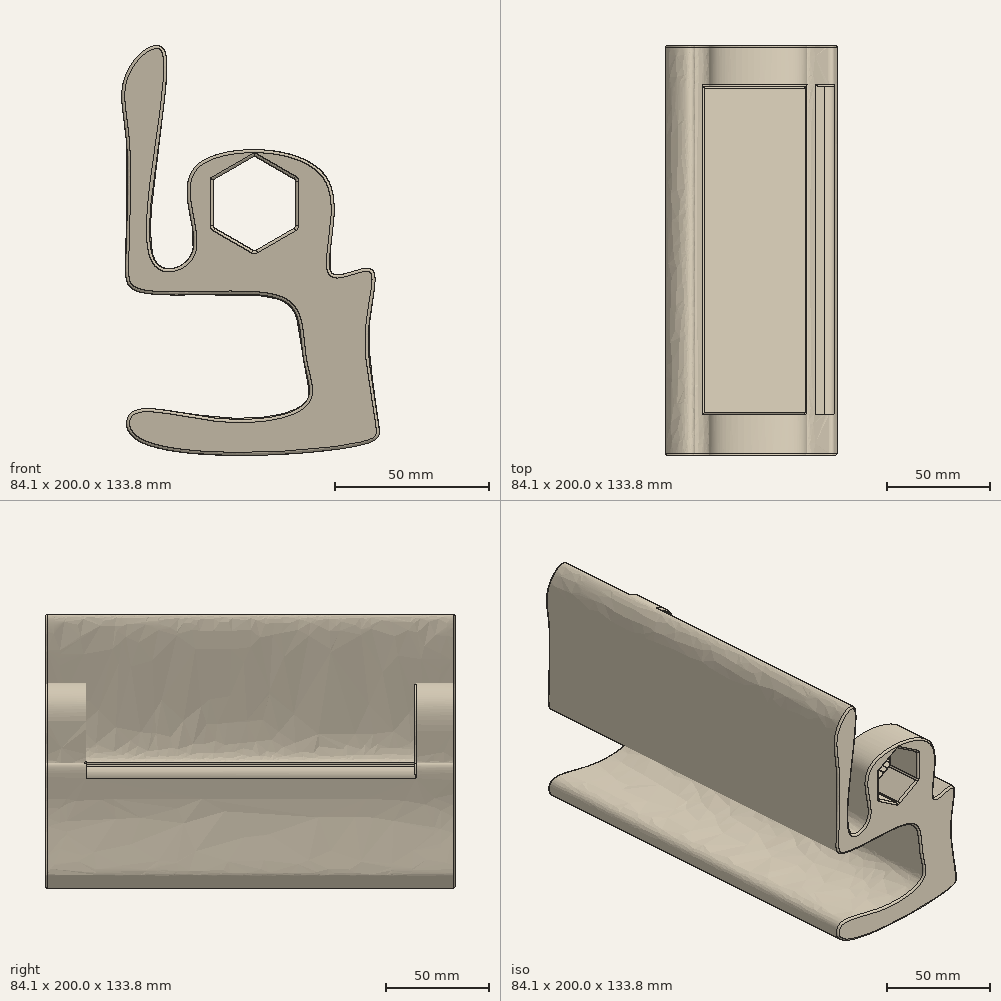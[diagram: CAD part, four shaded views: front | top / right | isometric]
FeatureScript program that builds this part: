
annotation { "Feature Type Name" : "Feature", "Feature Type Description" : "" }
export const myFeature = defineFeature(function(context is Context, id is Id, definition is map)
    precondition{}
    {
        {
            var Q0;
            Q0=qCreatedBy(makeId("Front.planeOp"),FACE);
            var sketch = newSketch(context, id + "F0", { "sketchPlane" : qUnion([Q0])});
            skFitSpline(sketch, "E0", {"points": [v(-28.85, 42.52) * mm, v(-29.24, 2.6) * mm, v(-25.85, -5.59) * mm, v(12.28, -6.79) * mm, v(26.05, -12.58) * mm, v(29.04, -29.14) * mm, v(29.84, -41.72) * mm, v(1.5, -47.3) * mm, v(-27.05, -45.31) * mm, v(-25.45, -54.3) * mm, v(50.8, -55.1) * mm, v(53.6, -51.9) * mm, v(53, -46.51) * mm, v(50.8, -32.94) * mm, v(50.6, -13.57) * mm, v(50.6, 1.6) * mm, v(38.34, 0) * mm, v(36.68, 30.86) * mm, v(-4.4, 36.56) * mm, v(-8.28, 19.56) * mm, v(-8.68, 4.6) * mm, v(-19.66, 4.2) * mm, v(-16.47, 72.66) * mm, v(-23.26, 72.66) * mm, v(-30.24, 61.08) * mm, v(-28.85, 42.52) * mm]});
            skSolve(sketch);
        }
        {
            var Q0;
            Q0=makeQuery(id+"F0.imprint","IMPRINT",FACE,{"disambiguationData":[TD([[makeQuery(id+"F0.imprint","IMPRINT",EDGE,{"derivedFrom":sQuery(id+"F0.wireOp",EDGE,"E0")}),1.0]])]});
            extrude(context, id + "F1", {"entities" : qUnion([Q0]), "depth" : 200 * mm, "offsetDistance" : 25 * mm});
        }
        {
            var Q0;
            Q0=qCreatedBy(makeId("Front.planeOp"),FACE);
            var sketch = newSketch(context, id + "F2", { "sketchPlane" : qUnion([Q0])});
            skCircle(sketch, "E1.cCircle", {"center": v(12.93, 22.83) * mm, "radius": 13.43 * mm, "construction": true});
            skLineSegment(sketch, "E1.0", {"start": v(26.35, 30.58) * mm, "end": v(26.35, 15.08) * mm});
            skLineSegment(sketch, "E1.1", {"start": v(26.35, 15.08) * mm, "end": v(12.93, 7.32) * mm});
            skLineSegment(sketch, "E1.2", {"start": v(12.93, 7.32) * mm, "end": v(-0.5, 15.08) * mm});
            skLineSegment(sketch, "E1.3", {"start": v(-0.5, 15.08) * mm, "end": v(-0.5, 30.58) * mm});
            skLineSegment(sketch, "E1.4", {"start": v(-0.5, 30.58) * mm, "end": v(12.93, 38.34) * mm});
            skLineSegment(sketch, "E1.5", {"start": v(12.93, 38.34) * mm, "end": v(26.35, 30.58) * mm});
            skPoint(sketch, "E1.0.midPoint", {"position": v(26.35, 22.83) * mm});
            skSolve(sketch);
        }
        {
            var Q0;
            Q0 = qSketchRegion(id + "F2", true);
            extrude(context, id + "F3", {"entities" : qUnion([Q0]), "operationType" : NewBodyOperationType.REMOVE, "depth" : 300 * mm, "offsetDistance" : 25 * mm});
        }
        {
            var Q0;
            Q0=qCreatedBy(makeId("Front.planeOp"),FACE);
            cPlane(context, id + "F4", {"entities" : qUnion([Q0]), "cplaneType" : CPlaneType.OFFSET, "offset" : 20 * mm, "width" : 150 * mm, "height" : 150 * mm});
        }
        {
            var Q0;
            Q0=qCreatedBy(id+"F4.planeOp",FACE);
            var sketch = newSketch(context, id + "F5", { "sketchPlane" : qUnion([Q0])});
            skLineSegment(sketch, "E2.bottom", {"start": v(-12.25, 63.95) * mm, "end": v(66.03, 63.95) * mm});
            skLineSegment(sketch, "E2.top", {"start": v(-12.25, 0) * mm, "end": v(66.03, 0) * mm});
            skLineSegment(sketch, "E2.left", {"start": v(-12.25, 63.95) * mm, "end": v(-12.25, 0) * mm});
            skLineSegment(sketch, "E2.right", {"start": v(66.03, 63.95) * mm, "end": v(66.03, 0) * mm});
            skSolve(sketch);
        }
        {
            var Q0;
            Q0 = qSketchRegion(id + "F5", true);
            extrude(context, id + "F6", {"entities" : qUnion([Q0]), "operationType" : NewBodyOperationType.REMOVE, "depth" : 160 * mm, "offsetDistance" : 25 * mm});
        }
        {
            var Q0;
            {var subQ0=sQuery(id+"F5.wireOp",EDGE,"E2.left");var subQ1=sQuery(id+"F5.wireOp",EDGE,"E2.top");Q0=makeQuery(id+"F6.boolean.opBoolean","COPY",EDGE,{"disambiguationData":[TD([makeQuery(id+"F1.opExtrude","SWEPT_FACE",FACE,{"disambiguationData":[OSD([sQuery(id+"F0.wireOp",EDGE,"E0")])]}),makeQuery(id+"F6.opExtrude","CAP_FACE",FACE,{"disambiguationData":[OSD([sQuery(id+"F5.wireOp",EDGE,"E2.bottom"),subQ1,subQ0,sQuery(id+"F5.wireOp",EDGE,"E2.right")])],"isStart":false}),makeQuery(id+"F6.opExtrude","SWEPT_FACE",FACE,{"disambiguationData":[OSD([subQ1])]}),makeQuery(id+"F6.opExtrude","SWEPT_FACE",FACE,{"disambiguationData":[OSD([subQ0])]})])],"derivedFrom":makeQuery(id+"F6.opExtrude","CAP_EDGE",EDGE,{"disambiguationData":[OSD([subQ1])],"isStart":false})});}
            var Q1;
            {var subQ0=sQuery(id+"F5.wireOp",EDGE,"E2.right");var subQ1=sQuery(id+"F5.wireOp",EDGE,"E2.left");var subQ2=sQuery(id+"F5.wireOp",EDGE,"E2.top");var subQ3=sQuery(id+"F5.wireOp",EDGE,"E2.bottom");Q1=makeQuery(id+"F6.boolean.opBoolean","COPY",FACE,{"disambiguationData":[TD([makeQuery(id+"F1.opExtrude","SWEPT_FACE",FACE,{"disambiguationData":[OSD([sQuery(id+"F0.wireOp",EDGE,"E0")])]}),makeQuery(id+"F6.opExtrude","CAP_FACE",FACE,{"disambiguationData":[OSD([subQ3,subQ2,subQ1,subQ0])],"isStart":true}),makeQuery(id+"F6.opExtrude","CAP_FACE",FACE,{"disambiguationData":[OSD([subQ3,subQ2,subQ1,subQ0])],"isStart":false}),makeQuery(id+"F6.opExtrude","SWEPT_FACE",FACE,{"disambiguationData":[OSD([subQ1])]})])],"derivedFrom":makeQuery(id+"F6.opExtrude","SWEPT_FACE",FACE,{"disambiguationData":[OSD([subQ2])]})});}
            var Q2;
            Q2=makeQuery(id+"F1.opExtrude","CAP_FACE",FACE,{"disambiguationData":[OSD([sQuery(id+"F0.wireOp",EDGE,"E0")])],"isStart":false});
            var Q3;
            Q3=makeQuery(id+"F1.opExtrude","CAP_EDGE",EDGE,{"disambiguationData":[OSD([sQuery(id+"F0.wireOp",EDGE,"E0")])],"isStart":true});
            var Q4;
            Q4=makeQuery(id+"F6.boolean.opBoolean","SPLIT",FACE,{"disambiguationData":[TD([makeQuery(id+"F1.opExtrude","CAP_FACE",FACE,{"disambiguationData":[OSD([sQuery(id+"F0.wireOp",EDGE,"E0")])],"isStart":true})])],"derivedFrom":makeQuery(id+"F3.boolean.opBoolean","COPY",FACE,{"derivedFrom":makeQuery(id+"F3.opExtrude","SWEPT_FACE",FACE,{"disambiguationData":[OSD([sQuery(id+"F2.wireOp",EDGE,"E1.1")])]})})});
            var Q5;
            Q5=makeQuery(id+"F6.boolean.opBoolean","INTERSECT",EDGE,{"disambiguationData":[OD(0.0)],"derivedFrom":[makeQuery(id+"F1.opExtrude","SWEPT_FACE",FACE,{"disambiguationData":[OSD([sQuery(id+"F0.wireOp",EDGE,"E0")])]}),makeQuery(id+"F6.opExtrude","CAP_FACE",FACE,{"disambiguationData":[OSD([sQuery(id+"F5.wireOp",EDGE,"E2.bottom"),sQuery(id+"F5.wireOp",EDGE,"E2.top"),sQuery(id+"F5.wireOp",EDGE,"E2.left"),sQuery(id+"F5.wireOp",EDGE,"E2.right")])],"isStart":true})]});
            var Q6;
            Q6=makeQuery(id+"F6.boolean.opBoolean","INTERSECT",EDGE,{"derivedFrom":[makeQuery(id+"F3.boolean.opBoolean","COPY",FACE,{"derivedFrom":makeQuery(id+"F3.opExtrude","SWEPT_FACE",FACE,{"disambiguationData":[OSD([sQuery(id+"F2.wireOp",EDGE,"E1.4")])]})}),makeQuery(id+"F6.opExtrude","CAP_FACE",FACE,{"disambiguationData":[OSD([sQuery(id+"F5.wireOp",EDGE,"E2.bottom"),sQuery(id+"F5.wireOp",EDGE,"E2.top"),sQuery(id+"F5.wireOp",EDGE,"E2.left"),sQuery(id+"F5.wireOp",EDGE,"E2.right")])],"isStart":true})]});
            var Q7;
            Q7=makeQuery(id+"F6.boolean.opBoolean","SPLIT",FACE,{"disambiguationData":[TD([makeQuery(id+"F1.opExtrude","CAP_FACE",FACE,{"disambiguationData":[OSD([sQuery(id+"F0.wireOp",EDGE,"E0")])],"isStart":true})])],"derivedFrom":makeQuery(id+"F3.boolean.opBoolean","COPY",FACE,{"derivedFrom":makeQuery(id+"F3.opExtrude","SWEPT_FACE",FACE,{"disambiguationData":[OSD([sQuery(id+"F2.wireOp",EDGE,"E1.2")])]})})});
            var Q8;
            Q8=makeQuery(id+"F6.boolean.opBoolean","SPLIT",FACE,{"disambiguationData":[TD([makeQuery(id+"F1.opExtrude","CAP_FACE",FACE,{"disambiguationData":[OSD([sQuery(id+"F0.wireOp",EDGE,"E0")])],"isStart":false})])],"derivedFrom":makeQuery(id+"F3.boolean.opBoolean","COPY",FACE,{"derivedFrom":makeQuery(id+"F3.opExtrude","SWEPT_FACE",FACE,{"disambiguationData":[OSD([sQuery(id+"F2.wireOp",EDGE,"E1.2")])]})})});
            var Q9;
            Q9=makeQuery(id+"F6.boolean.opBoolean","SPLIT",FACE,{"disambiguationData":[TD([makeQuery(id+"F1.opExtrude","CAP_FACE",FACE,{"disambiguationData":[OSD([sQuery(id+"F0.wireOp",EDGE,"E0")])],"isStart":false})])],"derivedFrom":makeQuery(id+"F3.boolean.opBoolean","COPY",FACE,{"derivedFrom":makeQuery(id+"F3.opExtrude","SWEPT_FACE",FACE,{"disambiguationData":[OSD([sQuery(id+"F2.wireOp",EDGE,"E1.1")])]})})});
            var Q10;
            Q10=makeQuery(id+"F6.boolean.opBoolean","SPLIT",FACE,{"disambiguationData":[TD([makeQuery(id+"F1.opExtrude","CAP_FACE",FACE,{"disambiguationData":[OSD([sQuery(id+"F0.wireOp",EDGE,"E0")])],"isStart":false})])],"derivedFrom":makeQuery(id+"F3.boolean.opBoolean","COPY",FACE,{"derivedFrom":makeQuery(id+"F3.opExtrude","SWEPT_FACE",FACE,{"disambiguationData":[OSD([sQuery(id+"F2.wireOp",EDGE,"E1.0")])]})})});
            var Q11;
            Q11=makeQuery(id+"F6.boolean.opBoolean","INTERSECT",EDGE,{"derivedFrom":[makeQuery(id+"F3.boolean.opBoolean","COPY",FACE,{"derivedFrom":makeQuery(id+"F3.opExtrude","SWEPT_FACE",FACE,{"disambiguationData":[OSD([sQuery(id+"F2.wireOp",EDGE,"E1.5")])]})}),makeQuery(id+"F6.opExtrude","CAP_FACE",FACE,{"disambiguationData":[OSD([sQuery(id+"F5.wireOp",EDGE,"E2.bottom"),sQuery(id+"F5.wireOp",EDGE,"E2.top"),sQuery(id+"F5.wireOp",EDGE,"E2.left"),sQuery(id+"F5.wireOp",EDGE,"E2.right")])],"isStart":false})]});
            var Q12;
            Q12=makeQuery(id+"F6.boolean.opBoolean","INTERSECT",EDGE,{"derivedFrom":[makeQuery(id+"F3.boolean.opBoolean","COPY",FACE,{"derivedFrom":makeQuery(id+"F3.opExtrude","SWEPT_FACE",FACE,{"disambiguationData":[OSD([sQuery(id+"F2.wireOp",EDGE,"E1.4")])]})}),makeQuery(id+"F6.opExtrude","CAP_FACE",FACE,{"disambiguationData":[OSD([sQuery(id+"F5.wireOp",EDGE,"E2.bottom"),sQuery(id+"F5.wireOp",EDGE,"E2.top"),sQuery(id+"F5.wireOp",EDGE,"E2.left"),sQuery(id+"F5.wireOp",EDGE,"E2.right")])],"isStart":false})]});
            fillet(context, id + "F7", {"entities" : qUnion([Q0, Q1, Q2, Q3, Q4, Q5, Q6, Q7, Q8, Q9, Q10, Q11, Q12]), "radius" : 1 * mm, "tangentPropagation" : true, "allowEdgeOverflow" : false});
        }
        {
            var Q0;
            Q0=makeQuery(id+"F6.boolean.opBoolean","INTERSECT",EDGE,{"disambiguationData":[OD(2.0)],"derivedFrom":[makeQuery(id+"F1.opExtrude","SWEPT_FACE",FACE,{"disambiguationData":[OSD([sQuery(id+"F0.wireOp",EDGE,"E0")])]}),makeQuery(id+"F6.opExtrude","SWEPT_FACE",FACE,{"disambiguationData":[OSD([sQuery(id+"F5.wireOp",EDGE,"E2.top")])]})]});
            fillet(context, id + "F8", {"entities" : qUnion([Q0]), "radius" : 5 * mm, "tangentPropagation" : true, "allowEdgeOverflow" : false});
        }
    });
